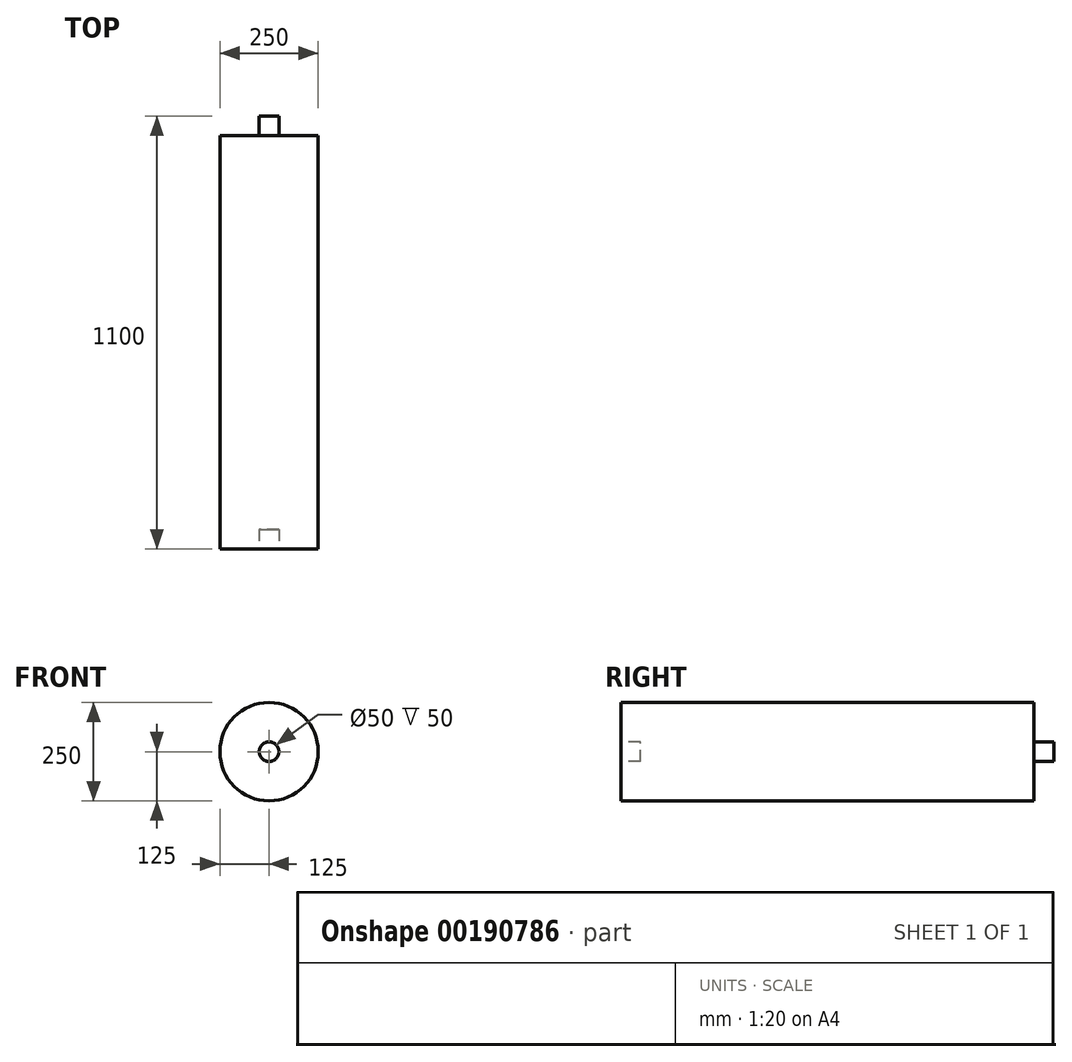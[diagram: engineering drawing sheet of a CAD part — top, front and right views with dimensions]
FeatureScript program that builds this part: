
annotation { "Feature Type Name" : "Feature", "Feature Type Description" : "" }
export const myFeature = defineFeature(function(context is Context, id is Id, definition is map)
    precondition{}
    {
        {
            var Q0;
            Q0=qCreatedBy(makeId("Front.planeOp"),FACE);
            var sketch = newSketch(context, id + "F0", { "sketchPlane" : qUnion([Q0])});
            skCircle(sketch, "E0", {"center": v(0, 0) * mm, "radius": 125 * mm});
            skSolve(sketch);
        }
        {
            var Q0;
            Q0 = qSketchRegion(id + "F0", true);
            extrude(context, id + "F1", {"entities" : qUnion([Q0]), "oppositeDirection" : true, "depth" : 1100 * mm});
        }
        {
            var Q0;
            Q0=makeQuery(id+"F1.opExtrude","CAP_FACE",FACE,{"disambiguationData":[OSD([sQuery(id+"F0.wireOp",EDGE,"E0")])],"isStart":true});
            var sketch = newSketch(context, id + "F2", { "sketchPlane" : qUnion([Q0])});
            skCircle(sketch, "E1", {"center": v(0, 0) * mm, "radius": 25 * mm});
            skSolve(sketch);
        }
        {
            var Q0;
            Q0 = qSketchRegion(id + "F2", true);
            extrude(context, id + "F3", {"entities" : qUnion([Q0]), "operationType" : NewBodyOperationType.REMOVE, "oppositeDirection" : true, "depth" : 50 * mm});
        }
        {
            var Q0;
            Q0=makeQuery(id+"F1.opExtrude","CAP_FACE",FACE,{"disambiguationData":[OSD([sQuery(id+"F0.wireOp",EDGE,"E0")])],"isStart":false});
            var sketch = newSketch(context, id + "F4", { "sketchPlane" : qUnion([Q0])});
            skCircle(sketch, "E2.0", {"center": v(0, 0) * mm, "radius": 25 * mm});
            skSolve(sketch);
        }
        {
            var Q0;
            Q0=makeQuery(id+"F4.imprint","IMPRINT",FACE,{"disambiguationData":[TD([[makeQuery(id+"F4.imprint","IMPRINT",EDGE,{"derivedFrom":sQuery(id+"F4.wireOp",EDGE,"E2.0")}),-1.0]])]});
            extrude(context, id + "F5", {"entities" : qUnion([Q0]), "operationType" : NewBodyOperationType.REMOVE, "oppositeDirection" : true, "depth" : 50 * mm});
        }
    });
